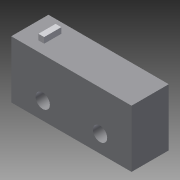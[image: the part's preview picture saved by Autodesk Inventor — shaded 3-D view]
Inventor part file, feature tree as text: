
AUTODESK INVENTOR PART (.ipt)
format: ipt  version: 2013 SP2 (Build 170200200, 200)  size: 92,160 bytes
history: native  units: mm
features: extrude x3, sketch x3
ambient origin geometry x8: Origin, YZ Plane, XZ Plane, XY Plane, X Axis, Y Axis, Z Axis, Center Point
bodies: Solid1 (feature_tree)
feature tree (6):
  extrude  "Extrusion1"  Depth=6.5mm
  extrude  "Extrusion2"  Depth=1.0mm
  extrude  "Extrusion3"  Depth=3.0mm
  sketch  "Sketch1"  dims[d0=21.0mm d1=6.5mm]
  sketch  "Sketch2"  dims[d2=10.0mm d3=0.0mm d4=1.0mm]
  sketch  "Sketch3"  dims[d5=3.0mm d6=3.0mm d7=1.0mm d8=0.0mm d9=2.5mm d10=2.5mm d11=3.0mm d12=10.0mm d13=2.0mm d14=0.0mm]
